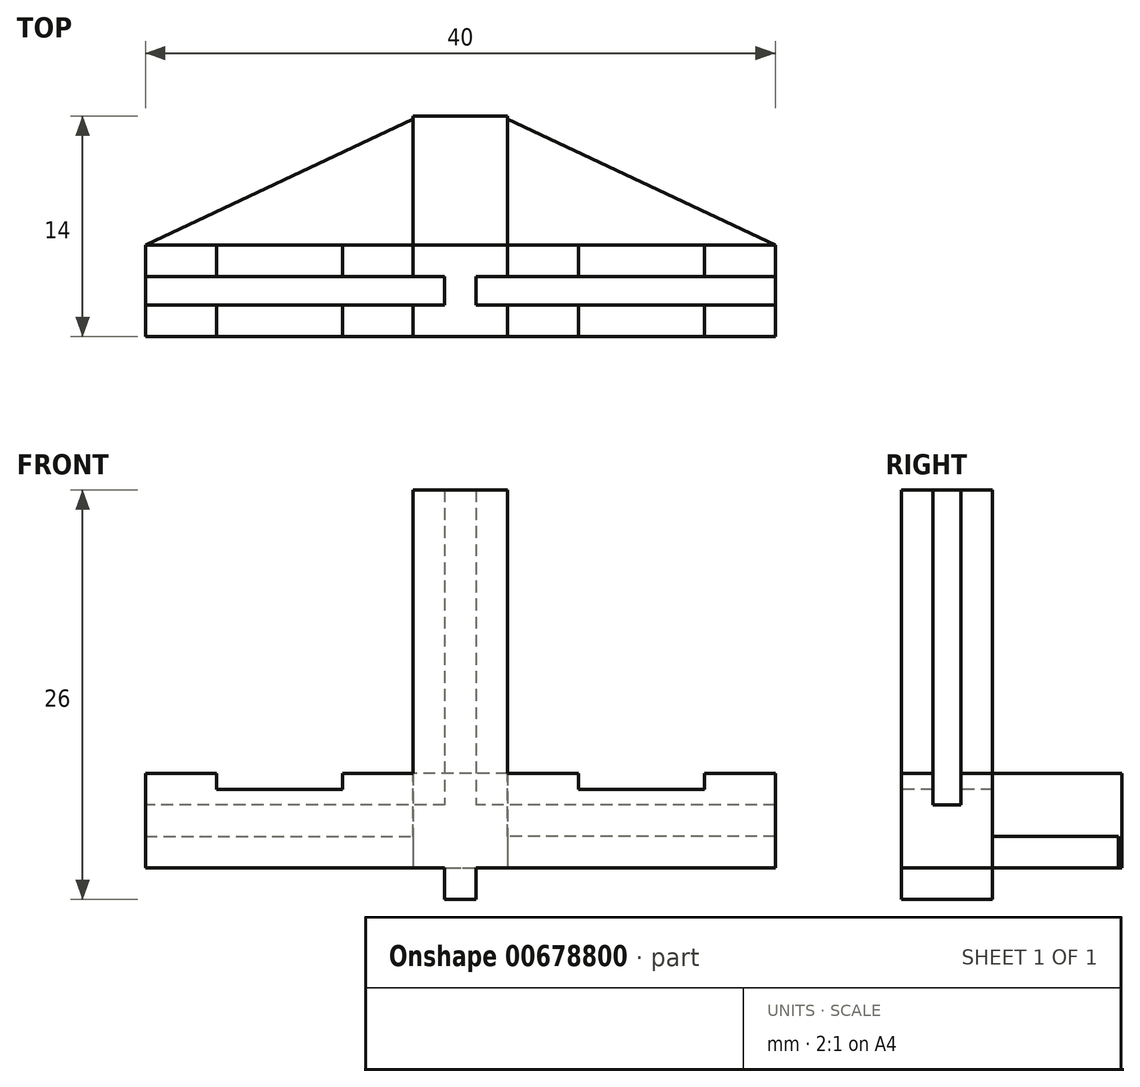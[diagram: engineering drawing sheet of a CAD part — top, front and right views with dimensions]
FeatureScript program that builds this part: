
annotation { "Feature Type Name" : "Feature", "Feature Type Description" : "" }
export const myFeature = defineFeature(function(context is Context, id is Id, definition is map)
    precondition{}
    {
        {
            var Q0;
            Q0=qCreatedBy(makeId("Top.planeOp"),FACE);
            var sketch = newSketch(context, id + "F0", { "sketchPlane" : qUnion([Q0])});
            skLineSegment(sketch, "E0.bottom", {"start": v(0, 0) * mm, "end": v(20, 0) * mm});
            skLineSegment(sketch, "E0.top", {"start": v(0, -5.8) * mm, "end": v(20, -5.8) * mm});
            skLineSegment(sketch, "E0.left", {"start": v(0, 0) * mm, "end": v(0, -5.8) * mm});
            skLineSegment(sketch, "E1", {"start": v(0, 0) * mm, "end": v(0, -2) * mm, "construction": true});
            skLineSegment(sketch, "E2", {"start": v(0, -3.8) * mm, "end": v(0, -5.8) * mm, "construction": true});
            skLineSegment(sketch, "E3", {"start": v(0, -3.8) * mm, "end": v(20, -3.8) * mm});
            skLineSegment(sketch, "E4", {"start": v(20, -2) * mm, "end": v(0, -2) * mm});
            skLineSegment(sketch, "E5", {"start": v(20, 0) * mm, "end": v(18, 0) * mm, "construction": true});
            skLineSegment(sketch, "E6", {"start": v(20, -5.8) * mm, "end": v(17, -5.8) * mm, "construction": true});
            skLineSegment(sketch, "E7", {"start": v(17, -5.8) * mm, "end": v(19, -5.8) * mm, "construction": true});
            skLineSegment(sketch, "E8", {"start": v(17, -5.8) * mm, "end": v(17, 0) * mm});
            skLineSegment(sketch, "E9.MirrorCS", {"start": v(20, -2) * mm, "end": v(40, -2) * mm});
            skLineSegment(sketch, "E10.MirrorCS", {"start": v(20, -5.8) * mm, "end": v(23, -5.8) * mm, "construction": true});
            skLineSegment(sketch, "E11.MirrorCS", {"start": v(40, 0) * mm, "end": v(40, -2) * mm, "construction": true});
            skLineSegment(sketch, "E12.MirrorCS", {"start": v(40, -5.8) * mm, "end": v(20, -5.8) * mm});
            skLineSegment(sketch, "E13.MirrorCS", {"start": v(23, -5.8) * mm, "end": v(21, -5.8) * mm, "construction": true});
            skLineSegment(sketch, "E14.MirrorCS", {"start": v(23, -5.8) * mm, "end": v(23, 0) * mm});
            skLineSegment(sketch, "E15.MirrorCS", {"start": v(40, -3.8) * mm, "end": v(20, -3.8) * mm});
            skLineSegment(sketch, "E16.MirrorCS", {"start": v(40, 0) * mm, "end": v(20, 0) * mm});
            skLineSegment(sketch, "E17.MirrorCS", {"start": v(20, 0) * mm, "end": v(22, 0) * mm, "construction": true});
            skLineSegment(sketch, "E18.MirrorCS", {"start": v(40, -3.8) * mm, "end": v(40, -5.8) * mm, "construction": true});
            skLineSegment(sketch, "E19.MirrorCS", {"start": v(40, 0) * mm, "end": v(40, -5.8) * mm});
            skLineSegment(sketch, "E20.bottom", {"start": v(17, 0) * mm, "end": v(23, 0) * mm});
            skLineSegment(sketch, "E20.top", {"start": v(17, 8) * mm, "end": v(23, 8) * mm});
            skLineSegment(sketch, "E20.left", {"start": v(17, 0) * mm, "end": v(17, 8) * mm});
            skLineSegment(sketch, "E20.right", {"start": v(23, 0) * mm, "end": v(23, 8) * mm});
            skLineSegment(sketch, "E21", {"start": v(21, -5.8) * mm, "end": v(21, 8) * mm});
            skLineSegment(sketch, "E22", {"start": v(19, -5.8) * mm, "end": v(19, 8) * mm});
            skLineSegment(sketch, "E23", {"start": v(17, 8) * mm, "end": v(17, 0) * mm});
            skLineSegment(sketch, "E24", {"start": v(17, 8) * mm, "end": v(0, 0) * mm});
            skLineSegment(sketch, "E25", {"start": v(40, 0) * mm, "end": v(23, 8) * mm});
            skSolve(sketch);
        }
        {
            var Q0;
            {var subQ0=sQuery(id+"F0.wireOp",EDGE,"E22");var subQ1=sQuery(id+"F0.wireOp",EDGE,"E4");var subQ2=makeQuery(id+"F0.imprint","INTERSECT",VERTEX,{"derivedFrom":[subQ1,subQ0]});Q0=makeQuery(id+"F0.imprint","IMPRINT",FACE,{"disambiguationData":[TD([[makeQuery(id+"F0.imprint","IMPRINT",EDGE,{"disambiguationData":[TD([[subQ2,-1.0]])],"derivedFrom":subQ1}),-1.0]])]});}
            var Q1;
            {var subQ1=sQuery(id+"F0.wireOp",EDGE,"E9.MirrorCS");var subQ7=sQuery(id+"F0.wireOp",EDGE,"E4");var subQ8=makeQuery(id+"F0.imprint","INTERSECT",VERTEX,{"derivedFrom":[subQ7,subQ1]});Q1=makeQuery(id+"F0.imprint","IMPRINT",FACE,{"disambiguationData":[TD([[makeQuery(id+"F0.imprint","IMPRINT",EDGE,{"disambiguationData":[TD([[subQ8,-1.0]])],"derivedFrom":subQ7}),-1.0]])]});}
            var Q2;
            {var subQ0=sQuery(id+"F0.wireOp",EDGE,"E21");var subQ1=sQuery(id+"F0.wireOp",EDGE,"E9.MirrorCS");var subQ2=makeQuery(id+"F0.imprint","INTERSECT",VERTEX,{"derivedFrom":[subQ1,subQ0]});Q2=makeQuery(id+"F0.imprint","IMPRINT",FACE,{"disambiguationData":[TD([[makeQuery(id+"F0.imprint","IMPRINT",EDGE,{"disambiguationData":[TD([[subQ2,-1.0]])],"derivedFrom":subQ1}),1.0]])]});}
            var Q3;
            {var subQ0=sQuery(id+"F0.wireOp",EDGE,"E15.MirrorCS");var subQ1=sQuery(id+"F0.wireOp",EDGE,"E3");var subQ2=makeQuery(id+"F0.imprint","INTERSECT",VERTEX,{"derivedFrom":[subQ1,subQ0]});Q3=makeQuery(id+"F0.imprint","IMPRINT",FACE,{"disambiguationData":[TD([[makeQuery(id+"F0.imprint","IMPRINT",EDGE,{"disambiguationData":[TD([[subQ2,1.0]])],"derivedFrom":subQ1}),1.0]])]});}
            var Q4;
            {var subQ0=sQuery(id+"F0.wireOp",EDGE,"E8");var subQ1=sQuery(id+"F0.wireOp",EDGE,"E0.top");var subQ2=makeQuery(id+"F0.imprint","INTERSECT",VERTEX,{"derivedFrom":[subQ1,subQ0]});Q4=makeQuery(id+"F0.imprint","IMPRINT",FACE,{"disambiguationData":[TD([[makeQuery(id+"F0.imprint","IMPRINT",EDGE,{"disambiguationData":[TD([[subQ2,-1.0]])],"derivedFrom":subQ1}),1.0]])]});}
            var Q5;
            {var subQ5=sQuery(id+"F0.wireOp",EDGE,"E12.MirrorCS");var subQ6=sQuery(id+"F0.wireOp",EDGE,"E0.top");var subQ7=makeQuery(id+"F0.imprint","INTERSECT",VERTEX,{"derivedFrom":[subQ6,subQ5]});Q5=makeQuery(id+"F0.imprint","IMPRINT",FACE,{"disambiguationData":[TD([[makeQuery(id+"F0.imprint","IMPRINT",EDGE,{"disambiguationData":[TD([[subQ7,1.0]])],"derivedFrom":subQ6}),1.0]])]});}
            var Q6;
            {var subQ0=sQuery(id+"F0.wireOp",EDGE,"E14.MirrorCS");var subQ1=sQuery(id+"F0.wireOp",EDGE,"E12.MirrorCS");var subQ2=makeQuery(id+"F0.imprint","INTERSECT",VERTEX,{"derivedFrom":[subQ1,subQ0]});Q6=makeQuery(id+"F0.imprint","IMPRINT",FACE,{"disambiguationData":[TD([[makeQuery(id+"F0.imprint","IMPRINT",EDGE,{"disambiguationData":[TD([[subQ2,-1.0]])],"derivedFrom":subQ1}),-1.0]])]});}
            extrude(context, id + "F1", {"entities" : qUnion([Q0, Q1, Q2, Q3, Q4, Q5, Q6]), "depth" : 24 * mm, "offsetDistance" : 25 * mm});
        }
        {
            var Q0;
            {var subQ0=sQuery(id+"F0.wireOp",EDGE,"E0.bottom");Q0=makeQuery(id+"F0.imprint","IMPRINT",FACE,{"disambiguationData":[TD([[makeQuery(id+"F0.imprint","IMPRINT",EDGE,{"derivedFrom":subQ0}),-1.0]])]});}
            var Q1;
            {var subQ0=sQuery(id+"F0.wireOp",EDGE,"E0.left");var subQ1=sQuery(id+"F0.wireOp",EDGE,"E0.top");var subQ2=makeQuery(id+"F0.imprint","INTERSECT",VERTEX,{"derivedFrom":[subQ1,subQ0]});Q1=makeQuery(id+"F0.imprint","IMPRINT",FACE,{"disambiguationData":[TD([[makeQuery(id+"F0.imprint","IMPRINT",EDGE,{"disambiguationData":[TD([[subQ2,-1.0]])],"derivedFrom":subQ1}),1.0]])]});}
            var Q2;
            {var subQ5=sQuery(id+"F0.wireOp",EDGE,"E16.MirrorCS");Q2=makeQuery(id+"F0.imprint","IMPRINT",FACE,{"disambiguationData":[TD([[makeQuery(id+"F0.imprint","IMPRINT",EDGE,{"derivedFrom":subQ5}),1.0]])]});}
            var Q3;
            {var subQ0=sQuery(id+"F0.wireOp",EDGE,"E19.MirrorCS");var subQ1=sQuery(id+"F0.wireOp",EDGE,"E12.MirrorCS");var subQ2=makeQuery(id+"F0.imprint","INTERSECT",VERTEX,{"derivedFrom":[subQ1,subQ0]});Q3=makeQuery(id+"F0.imprint","IMPRINT",FACE,{"disambiguationData":[TD([[makeQuery(id+"F0.imprint","IMPRINT",EDGE,{"disambiguationData":[TD([[subQ2,-1.0]])],"derivedFrom":subQ1}),-1.0]])]});}
            extrude(context, id + "F2", {"entities" : qUnion([Q0, Q1, Q2, Q3]), "operationType" : NewBodyOperationType.ADD, "depth" : 6 * mm, "offsetDistance" : 25 * mm});
        }
        {
            var Q0;
            {var subQ0=sQuery(id+"F0.wireOp",EDGE,"E3");var subQ1=sQuery(id+"F0.wireOp",EDGE,"E0.left");var subQ2=makeQuery(id+"F0.imprint","INTERSECT",VERTEX,{"derivedFrom":[subQ1,subQ0]});Q0=makeQuery(id+"F0.imprint","IMPRINT",FACE,{"disambiguationData":[TD([[makeQuery(id+"F0.imprint","IMPRINT",EDGE,{"disambiguationData":[TD([[subQ2,1.0]])],"derivedFrom":subQ1}),1.0]])]});}
            var Q1;
            {var subQ0=sQuery(id+"F0.wireOp",EDGE,"E8");var subQ1=sQuery(id+"F0.wireOp",EDGE,"E3");var subQ2=makeQuery(id+"F0.imprint","INTERSECT",VERTEX,{"derivedFrom":[subQ1,subQ0]});Q1=makeQuery(id+"F0.imprint","IMPRINT",FACE,{"disambiguationData":[TD([[makeQuery(id+"F0.imprint","IMPRINT",EDGE,{"disambiguationData":[TD([[subQ2,-1.0]])],"derivedFrom":subQ1}),1.0]])]});}
            var Q2;
            {var subQ0=sQuery(id+"F0.wireOp",EDGE,"E21");var subQ1=sQuery(id+"F0.wireOp",EDGE,"E9.MirrorCS");var subQ2=makeQuery(id+"F0.imprint","INTERSECT",VERTEX,{"derivedFrom":[subQ1,subQ0]});Q2=makeQuery(id+"F0.imprint","IMPRINT",FACE,{"disambiguationData":[TD([[makeQuery(id+"F0.imprint","IMPRINT",EDGE,{"disambiguationData":[TD([[subQ2,-1.0]])],"derivedFrom":subQ1}),-1.0]])]});}
            var Q3;
            {var subQ0=sQuery(id+"F0.wireOp",EDGE,"E19.MirrorCS");var subQ1=sQuery(id+"F0.wireOp",EDGE,"E9.MirrorCS");var subQ2=makeQuery(id+"F0.imprint","INTERSECT",VERTEX,{"derivedFrom":[subQ1,subQ0]});Q3=makeQuery(id+"F0.imprint","IMPRINT",FACE,{"disambiguationData":[TD([[makeQuery(id+"F0.imprint","IMPRINT",EDGE,{"disambiguationData":[TD([[subQ2,1.0]])],"derivedFrom":subQ1}),-1.0]])]});}
            extrude(context, id + "F3", {"entities" : qUnion([Q0, Q1, Q2, Q3]), "operationType" : NewBodyOperationType.ADD, "depth" : 4 * mm, "offsetDistance" : 25 * mm});
        }
        {
            var Q0;
            {var subQ0=sQuery(id+"F0.wireOp",EDGE,"E12.MirrorCS");var subQ1=sQuery(id+"F0.wireOp",EDGE,"E0.top");Q0=makeQuery(id+"F2.boolean.opBoolean","MERGE",FACE,{"derivedFrom":[makeQuery(id+"F1.opExtrude","SWEPT_FACE",FACE,{"disambiguationData":[OSD([subQ1,subQ0])]}),makeQuery(id+"F2.opExtrude","SWEPT_FACE",FACE,{"disambiguationData":[OSD([subQ1])]}),makeQuery(id+"F2.opExtrude","SWEPT_FACE",FACE,{"disambiguationData":[OSD([subQ0])]})]});}
            var sketch = newSketch(context, id + "F4", { "sketchPlane" : qUnion([Q0])});
            skLineSegment(sketch, "E26.bottom", {"start": v(17, 6) * mm, "end": v(23, 6) * mm});
            skLineSegment(sketch, "E26.top", {"start": v(17, 0) * mm, "end": v(23, 0) * mm});
            skLineSegment(sketch, "E26.left", {"start": v(17, 6) * mm, "end": v(17, 0) * mm});
            skLineSegment(sketch, "E26.right", {"start": v(23, 6) * mm, "end": v(23, 0) * mm});
            skSolve(sketch);
        }
        {
            var Q0;
            Q0=makeQuery(id+"F4.imprint","IMPRINT",FACE,{"disambiguationData":[TD([[makeQuery(id+"F4.imprint","IMPRINT",EDGE,{"derivedFrom":sQuery(id+"F4.wireOp",EDGE,"E26.bottom")}),-1.0]])]});
            extrude(context, id + "F5", {"entities" : qUnion([Q0]), "operationType" : NewBodyOperationType.ADD, "depth" : -14 * mm, "offsetDistance" : 25 * mm});
        }
        {
            var Q0;
            {var subQ5=sQuery(id+"F0.wireOp",EDGE,"E12.MirrorCS");var subQ6=sQuery(id+"F0.wireOp",EDGE,"E0.top");var subQ7=makeQuery(id+"F0.imprint","INTERSECT",VERTEX,{"derivedFrom":[subQ6,subQ5]});Q0=makeQuery(id+"F0.imprint","IMPRINT",FACE,{"disambiguationData":[TD([[makeQuery(id+"F0.imprint","IMPRINT",EDGE,{"disambiguationData":[TD([[subQ7,1.0]])],"derivedFrom":subQ6}),1.0]])]});}
            var Q1;
            {var subQ0=sQuery(id+"F0.wireOp",EDGE,"E15.MirrorCS");var subQ1=sQuery(id+"F0.wireOp",EDGE,"E3");var subQ2=makeQuery(id+"F0.imprint","INTERSECT",VERTEX,{"derivedFrom":[subQ1,subQ0]});Q1=makeQuery(id+"F0.imprint","IMPRINT",FACE,{"disambiguationData":[TD([[makeQuery(id+"F0.imprint","IMPRINT",EDGE,{"disambiguationData":[TD([[subQ2,1.0]])],"derivedFrom":subQ1}),1.0]])]});}
            var Q2;
            {var subQ1=sQuery(id+"F0.wireOp",EDGE,"E9.MirrorCS");var subQ7=sQuery(id+"F0.wireOp",EDGE,"E4");var subQ8=makeQuery(id+"F0.imprint","INTERSECT",VERTEX,{"derivedFrom":[subQ7,subQ1]});Q2=makeQuery(id+"F0.imprint","IMPRINT",FACE,{"disambiguationData":[TD([[makeQuery(id+"F0.imprint","IMPRINT",EDGE,{"disambiguationData":[TD([[subQ8,-1.0]])],"derivedFrom":subQ7}),-1.0]])]});}
            var Q3;
            {var subQ0=sQuery(id+"F0.wireOp",EDGE,"E22");var subQ1=sQuery(id+"F0.wireOp",EDGE,"E20.bottom");var subQ2=makeQuery(id+"F0.imprint","INTERSECT",VERTEX,{"derivedFrom":[subQ1,subQ0]});Q3=makeQuery(id+"F0.imprint","IMPRINT",FACE,{"disambiguationData":[TD([[makeQuery(id+"F0.imprint","IMPRINT",EDGE,{"disambiguationData":[TD([[subQ2,-1.0]])],"derivedFrom":subQ1}),1.0]])]});}
            extrude(context, id + "F6", {"entities" : qUnion([Q0, Q1, Q2, Q3]), "operationType" : NewBodyOperationType.ADD, "depth" : -2 * mm, "offsetDistance" : 25 * mm});
        }
        {
            var Q0;
            {var subQ5=sQuery(id+"F0.wireOp",EDGE,"E3");Q0=makeQuery(id+"F5.boolean.opBoolean","SPLIT",FACE,{"disambiguationData":[TD([makeQuery(id+"F1.opExtrude","SWEPT_FACE",FACE,{"disambiguationData":[OSD([subQ5])]})])],"derivedFrom":makeQuery(id+"F5.opExtrude","SWEPT_FACE",FACE,{"disambiguationData":[OSD([sQuery(id+"F4.wireOp",EDGE,"E26.left")])]})});}
            extrude(context, id + "F7", {"entities" : qUnion([Q0]), "operationType" : NewBodyOperationType.REMOVE, "oppositeDirection" : true, "depth" : 2 * mm, "offsetDistance" : 25 * mm});
        }
        {
            var Q0;
            {var subQ5=sQuery(id+"F0.wireOp",EDGE,"E9.MirrorCS");Q0=makeQuery(id+"F5.boolean.opBoolean","SPLIT",FACE,{"disambiguationData":[TD([makeQuery(id+"F1.opExtrude","SWEPT_FACE",FACE,{"disambiguationData":[OSD([subQ5])]})])],"derivedFrom":makeQuery(id+"F5.opExtrude","SWEPT_FACE",FACE,{"disambiguationData":[OSD([sQuery(id+"F4.wireOp",EDGE,"E26.right")])]})});}
            extrude(context, id + "F8", {"entities" : qUnion([Q0]), "operationType" : NewBodyOperationType.REMOVE, "oppositeDirection" : true, "depth" : 2 * mm, "offsetDistance" : 25 * mm});
        }
        {
            var Q0;
            {var subQ0=sQuery(id+"F0.wireOp",EDGE,"E12.MirrorCS");var subQ1=sQuery(id+"F0.wireOp",EDGE,"E0.top");Q0=makeQuery(id+"F6.boolean.opBoolean","MERGE",FACE,{"derivedFrom":[makeQuery(id+"F2.boolean.opBoolean","MERGE",FACE,{"derivedFrom":[makeQuery(id+"F1.opExtrude","SWEPT_FACE",FACE,{"disambiguationData":[OSD([subQ1,subQ0])]}),makeQuery(id+"F2.opExtrude","SWEPT_FACE",FACE,{"disambiguationData":[OSD([subQ1])]}),makeQuery(id+"F2.opExtrude","SWEPT_FACE",FACE,{"disambiguationData":[OSD([subQ0])]})]}),makeQuery(id+"F6.opExtrude","SWEPT_FACE",FACE,{"disambiguationData":[OSD([subQ1,subQ0])]})]});}
            var sketch = newSketch(context, id + "F9", { "sketchPlane" : qUnion([Q0])});
            skLineSegment(sketch, "E27", {"start": v(0, 6) * mm, "end": v(17, 6) * mm, "construction": true});
            skLineSegment(sketch, "E28", {"start": v(17, 6) * mm, "end": v(23, 6) * mm, "construction": true});
            skLineSegment(sketch, "E29", {"start": v(23, 6) * mm, "end": v(40, 6) * mm, "construction": true});
            skLineSegment(sketch, "E30.bottom", {"start": v(12.5, 5) * mm, "end": v(4.5, 5) * mm});
            skLineSegment(sketch, "E30.top", {"start": v(12.5, 7) * mm, "end": v(4.5, 7) * mm});
            skLineSegment(sketch, "E30.left", {"start": v(12.5, 5) * mm, "end": v(12.5, 7) * mm});
            skLineSegment(sketch, "E30.right", {"start": v(4.5, 5) * mm, "end": v(4.5, 7) * mm});
            skPoint(sketch, "E30.middle", {"position": v(8.5, 6) * mm});
            skLineSegment(sketch, "E31.bottom", {"start": v(35.5, 5) * mm, "end": v(27.5, 5) * mm});
            skLineSegment(sketch, "E31.top", {"start": v(35.5, 7) * mm, "end": v(27.5, 7) * mm});
            skLineSegment(sketch, "E31.left", {"start": v(35.5, 5) * mm, "end": v(35.5, 7) * mm});
            skLineSegment(sketch, "E31.right", {"start": v(27.5, 5) * mm, "end": v(27.5, 7) * mm});
            skPoint(sketch, "E31.middle", {"position": v(31.5, 6) * mm});
            skSolve(sketch);
        }
        {
            var Q0;
            {var subQ0=sQuery(id+"F9.wireOp",EDGE,"E30.bottom");Q0=makeQuery(id+"F9.imprint","IMPRINT",FACE,{"disambiguationData":[TD([[makeQuery(id+"F9.imprint","IMPRINT",EDGE,{"derivedFrom":subQ0}),-1.0]])]});}
            var Q1;
            {var subQ0=sQuery(id+"F9.wireOp",EDGE,"E30.top");Q1=makeQuery(id+"F9.imprint","IMPRINT",FACE,{"disambiguationData":[TD([[makeQuery(id+"F9.imprint","IMPRINT",EDGE,{"derivedFrom":subQ0}),1.0]])]});}
            var Q2;
            {var subQ0=sQuery(id+"F9.wireOp",EDGE,"E31.top");Q2=makeQuery(id+"F9.imprint","IMPRINT",FACE,{"disambiguationData":[TD([[makeQuery(id+"F9.imprint","IMPRINT",EDGE,{"derivedFrom":subQ0}),1.0]])]});}
            var Q3;
            {var subQ0=sQuery(id+"F9.wireOp",EDGE,"E31.bottom");Q3=makeQuery(id+"F9.imprint","IMPRINT",FACE,{"disambiguationData":[TD([[makeQuery(id+"F9.imprint","IMPRINT",EDGE,{"derivedFrom":subQ0}),-1.0]])]});}
            extrude(context, id + "F10", {"entities" : qUnion([Q0, Q1, Q2, Q3]), "operationType" : NewBodyOperationType.REMOVE, "oppositeDirection" : true, "depth" : 6 * mm, "offsetDistance" : 25 * mm});
        }
        {
            var Q0;
            Q0=makeQuery(id+"F0.imprint","IMPRINT",FACE,{"disambiguationData":[TD([[makeQuery(id+"F0.imprint","IMPRINT",EDGE,{"derivedFrom":sQuery(id+"F0.wireOp",EDGE,"E0.bottom")}),1.0]])]});
            extrude(context, id + "F11", {"entities" : qUnion([Q0]), "operationType" : NewBodyOperationType.ADD, "depth" : 2 * mm, "offsetDistance" : 25 * mm});
        }
        {
            var Q0;
            Q0=makeQuery(id+"F0.imprint","IMPRINT",FACE,{"disambiguationData":[TD([[makeQuery(id+"F0.imprint","IMPRINT",EDGE,{"derivedFrom":sQuery(id+"F0.wireOp",EDGE,"E16.MirrorCS")}),-1.0]])]});
            extrude(context, id + "F12", {"entities" : qUnion([Q0]), "operationType" : NewBodyOperationType.ADD, "depth" : 2 * mm, "offsetDistance" : 25 * mm});
        }
    });
